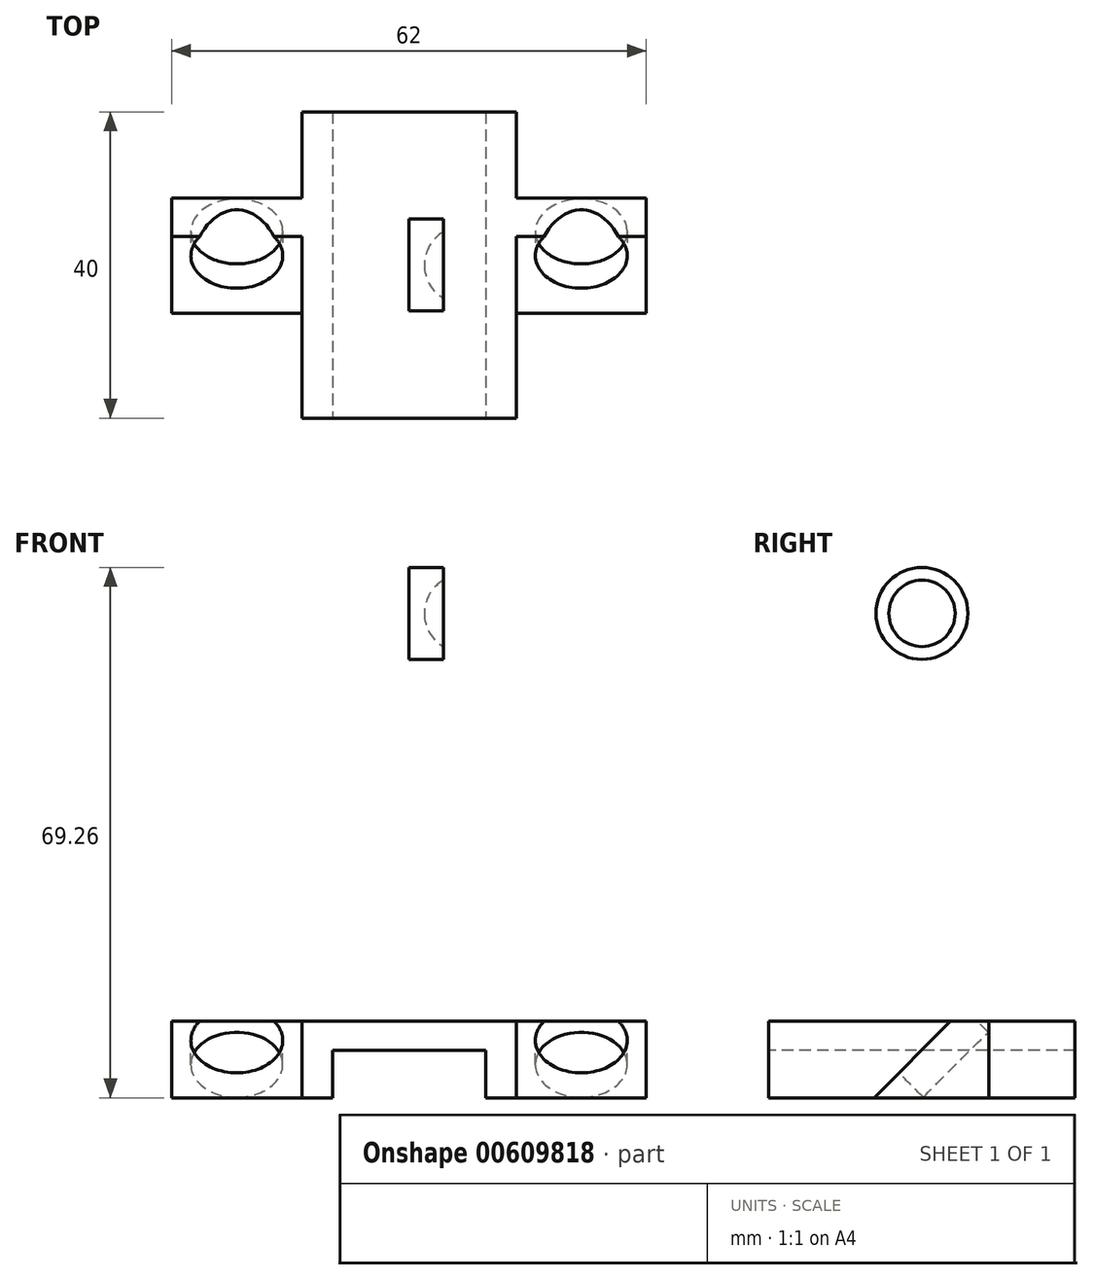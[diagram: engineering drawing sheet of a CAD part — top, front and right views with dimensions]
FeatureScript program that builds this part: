
annotation { "Feature Type Name" : "Feature", "Feature Type Description" : "" }
export const myFeature = defineFeature(function(context is Context, id is Id, definition is map)
    precondition{}
    {
        {
            var Q0;
            Q0=qCreatedBy(makeId("Top.planeOp"),FACE);
            var sketch = newSketch(context, id + "F0", { "sketchPlane" : qUnion([Q0])});
            skLineSegment(sketch, "E0.bottom", {"start": v(14, 20) * mm, "end": v(-14, 20) * mm});
            skLineSegment(sketch, "E0.top", {"start": v(14, -20) * mm, "end": v(-14, -20) * mm});
            skLineSegment(sketch, "E0.left", {"start": v(14, 20) * mm, "end": v(14, 8.72) * mm});
            skLineSegment(sketch, "E0.right", {"start": v(-14, 20) * mm, "end": v(-14, 8.72) * mm});
            skPoint(sketch, "E0.middle", {"position": v(0, 0) * mm});
            skLineSegment(sketch, "E1.bottom", {"start": v(-31, -6.28) * mm, "end": v(-14, -6.28) * mm});
            skLineSegment(sketch, "E1.top", {"start": v(-31, 8.72) * mm, "end": v(-14, 8.72) * mm});
            skLineSegment(sketch, "E1.left", {"start": v(-31, -6.28) * mm, "end": v(-31, 8.72) * mm});
            skLineSegment(sketch, "E1.right", {"start": v(31, -6.28) * mm, "end": v(31, 8.72) * mm});
            skLineSegment(sketch, "E2.trimOffspring", {"start": v(14, 8.72) * mm, "end": v(31, 8.72) * mm});
            skLineSegment(sketch, "E3.trimOffspring", {"start": v(-14, -6.28) * mm, "end": v(-14, -20) * mm});
            skLineSegment(sketch, "E4.trimOffspring", {"start": v(14, -6.28) * mm, "end": v(31, -6.28) * mm});
            skLineSegment(sketch, "E5.trimOffspring", {"start": v(14, -6.28) * mm, "end": v(14, -20) * mm});
            skSolve(sketch);
        }
        {
            var Q0;
            Q0=makeQuery(id+"F0.imprint","IMPRINT",FACE,{"disambiguationData":[TD([[makeQuery(id+"F0.imprint","IMPRINT",EDGE,{"derivedFrom":sQuery(id+"F0.wireOp",EDGE,"E0.bottom")}),1.0]])]});
            extrude(context, id + "F1", {"entities" : qUnion([Q0]), "depth" : 10 * mm, "offsetDistance" : 25 * mm});
        }
        {
            var Q0;
            Q0=makeQuery(id+"F1.opExtrude","SWEPT_FACE",FACE,{"disambiguationData":[OSD([sQuery(id+"F0.wireOp",EDGE,"E0.top")])]});
            var sketch = newSketch(context, id + "F2", { "sketchPlane" : qUnion([Q0])});
            skLineSegment(sketch, "E6.bottom", {"start": v(-10, 0) * mm, "end": v(10, 0) * mm});
            skLineSegment(sketch, "E6.top", {"start": v(-10, 6.21) * mm, "end": v(10, 6.21) * mm});
            skLineSegment(sketch, "E6.left", {"start": v(-10, 0) * mm, "end": v(-10, 6.21) * mm});
            skLineSegment(sketch, "E6.right", {"start": v(10, 0) * mm, "end": v(10, 6.21) * mm});
            skSolve(sketch);
        }
        {
            var Q0;
            Q0=makeQuery(id+"F2.imprint","IMPRINT",FACE,{"disambiguationData":[TD([[makeQuery(id+"F2.imprint","IMPRINT",EDGE,{"derivedFrom":sQuery(id+"F2.wireOp",EDGE,"E6.bottom")}),-1.0]])]});
            extrude(context, id + "F3", {"entities" : qUnion([Q0]), "operationType" : NewBodyOperationType.REMOVE, "endBound" : BoundingType.THROUGH_ALL, "oppositeDirection" : true, "depth" : 25 * mm, "offsetDistance" : 25 * mm});
        }
        {
            var Q0;
            Q0=makeQuery(id+"F1.opExtrude","SWEPT_FACE",FACE,{"disambiguationData":[OSD([sQuery(id+"F0.wireOp",EDGE,"E1.right")])]});
            var sketch = newSketch(context, id + "F4", { "sketchPlane" : qUnion([Q0])});
            skLineSegment(sketch, "E7", {"start": v(-6.28, 0) * mm, "end": v(3.72, 10) * mm});
            skLineSegment(sketch, "E8", {"start": v(-6.28, 0) * mm, "end": v(-6.28, 10) * mm});
            skLineSegment(sketch, "E9", {"start": v(-6.28, 10) * mm, "end": v(3.72, 10) * mm});
            skLineSegment(sketch, "E10", {"start": v(8.72, 0) * mm, "end": v(1.22, 7.5) * mm});
            skPoint(sketch, "E11", {"position": v(1.22, 7.5) * mm});
            skSolve(sketch);
        }
        {
            var Q0;
            Q0=makeQuery(id+"F4.imprint","IMPRINT",FACE,{"disambiguationData":[TD([[makeQuery(id+"F4.imprint","IMPRINT",EDGE,{"derivedFrom":sQuery(id+"F4.wireOp",EDGE,"E7")}),1.0]])]});
            extrude(context, id + "F5", {"entities" : qUnion([Q0]), "operationType" : NewBodyOperationType.REMOVE, "oppositeDirection" : true, "depth" : 17 * mm, "offsetDistance" : 25 * mm});
        }
        {
            var Q0;
            Q0=makeQuery(id+"F5.boolean.opBoolean","COPY",FACE,{"derivedFrom":makeQuery(id+"F5.opExtrude","SWEPT_FACE",FACE,{"disambiguationData":[OSD([sQuery(id+"F4.wireOp",EDGE,"E7")])]})});
            var sketch = newSketch(context, id + "F6", { "sketchPlane" : qUnion([Q0])});
            skPoint(sketch, "E12", {"position": v(22.5, 6.17) * mm});
            skLineSegment(sketch, "E13.0", {"start": v(31, 2.63) * mm, "end": v(31, 9.7) * mm});
            skLineSegment(sketch, "E14.0", {"start": v(14, 9.7) * mm, "end": v(31, 9.7) * mm});
            skCircle(sketch, "E15", {"center": v(22.5, 6.17) * mm, "radius": 6 * mm});
            skSolve(sketch);
        }
        {
            var Q0;
            {var subQ0=sQuery(id+"F6.wireOp",EDGE,"E15");var subQ1=sQuery(id+"F6.wireOp",EDGE,"E14.0");var subQ2=makeQuery(id+"F6.imprint","INTERSECT",VERTEX,{"disambiguationData":[OD(0.0)],"derivedFrom":[subQ1,subQ0]});Q0=makeQuery(id+"F6.imprint","IMPRINT",FACE,{"disambiguationData":[TD([[makeQuery(id+"F6.imprint","IMPRINT",EDGE,{"disambiguationData":[TD([[subQ2,-1.0]])],"derivedFrom":subQ1}),-1.0]])]});}
            var Q1;
            {var subQ0=sQuery(id+"F6.wireOp",EDGE,"E15");var subQ1=sQuery(id+"F6.wireOp",EDGE,"E14.0");var subQ2=makeQuery(id+"F6.imprint","INTERSECT",VERTEX,{"disambiguationData":[OD(0.0)],"derivedFrom":[subQ1,subQ0]});Q1=makeQuery(id+"F6.imprint","IMPRINT",FACE,{"disambiguationData":[TD([[makeQuery(id+"F6.imprint","IMPRINT",EDGE,{"disambiguationData":[TD([[subQ2,-1.0]])],"derivedFrom":subQ1}),1.0]])]});}
            extrude(context, id + "F7", {"entities" : qUnion([Q0, Q1]), "operationType" : NewBodyOperationType.REMOVE, "oppositeDirection" : true, "depth" : 4.5 * mm, "offsetDistance" : 25 * mm});
        }
        {
            var Q0;
            Q0=makeQuery(id+"F1.opExtrude","SWEPT_FACE",FACE,{"disambiguationData":[OSD([sQuery(id+"F0.wireOp",EDGE,"E1.left")])]});
            var sketch = newSketch(context, id + "F8", { "sketchPlane" : qUnion([Q0])});
            skLineSegment(sketch, "E16", {"start": v(6.28, 0) * mm, "end": v(-3.72, 10) * mm});
            skLineSegment(sketch, "E17", {"start": v(-8.72, 0) * mm, "end": v(-1.22, 7.5) * mm});
            skPoint(sketch, "E18", {"position": v(-3.72, 10) * mm});
            skSolve(sketch);
        }
        {
            var Q0;
            {var subQ1=sQuery(id+"F0.wireOp",EDGE,"E1.left");var subQ2=makeQuery(id+"F1.opExtrude","SWEPT_EDGE",EDGE,{"disambiguationData":[OSD([sQuery(id+"F0.wireOp",EDGE,"E1.bottom"),subQ1])]});Q0=makeQuery(id+"F8.imprint","IMPRINT",FACE,{"disambiguationData":[TD([[makeQuery(id+"F8.imprint","IMPRINT",EDGE,{"derivedFrom":subQ2}),-1.0]])]});}
            extrude(context, id + "F9", {"entities" : qUnion([Q0]), "operationType" : NewBodyOperationType.REMOVE, "oppositeDirection" : true, "depth" : 17 * mm, "offsetDistance" : 25 * mm});
        }
        {
            var Q0;
            Q0=makeQuery(id+"F9.boolean.opBoolean","COPY",FACE,{"derivedFrom":makeQuery(id+"F9.opExtrude","SWEPT_FACE",FACE,{"disambiguationData":[OSD([sQuery(id+"F8.wireOp",EDGE,"E16")])]})});
            var sketch = newSketch(context, id + "F10", { "sketchPlane" : qUnion([Q0])});
            skPoint(sketch, "E19", {"position": v(-22.5, 6.17) * mm});
            skCircle(sketch, "E20", {"center": v(-22.5, 6.17) * mm, "radius": 6 * mm});
            skSolve(sketch);
        }
        {
            var Q0;
            {var subQ0=sQuery(id+"F10.wireOp",EDGE,"E20");var subQ1=makeQuery(id+"F9.boolean.opBoolean","COPY",EDGE,{"derivedFrom":makeQuery(id+"F9.opExtrude","SWEPT_EDGE",EDGE,{"disambiguationData":[OSD([sQuery(id+"F0.wireOp",EDGE,"E1.left"),sQuery(id+"F8.wireOp",EDGE,"E16")])]})});var subQ2=makeQuery(id+"F10.imprint","INTERSECT",VERTEX,{"disambiguationData":[OD(0.0)],"derivedFrom":[subQ1,subQ0]});Q0=makeQuery(id+"F10.imprint","IMPRINT",FACE,{"disambiguationData":[TD([[makeQuery(id+"F10.imprint","IMPRINT",EDGE,{"disambiguationData":[TD([[subQ2,-1.0]])],"derivedFrom":subQ0}),1.0]])]});}
            var Q1;
            {var subQ0=sQuery(id+"F10.wireOp",EDGE,"E20");var subQ1=makeQuery(id+"F9.boolean.opBoolean","COPY",EDGE,{"derivedFrom":makeQuery(id+"F9.opExtrude","SWEPT_EDGE",EDGE,{"disambiguationData":[OSD([sQuery(id+"F0.wireOp",EDGE,"E1.left"),sQuery(id+"F8.wireOp",EDGE,"E16")])]})});var subQ2=makeQuery(id+"F10.imprint","INTERSECT",VERTEX,{"disambiguationData":[OD(0.0)],"derivedFrom":[subQ1,subQ0]});Q1=makeQuery(id+"F10.imprint","IMPRINT",FACE,{"disambiguationData":[TD([[makeQuery(id+"F10.imprint","IMPRINT",EDGE,{"disambiguationData":[TD([[subQ2,1.0]])],"derivedFrom":subQ0}),1.0]])]});}
            extrude(context, id + "F11", {"entities" : qUnion([Q0, Q1]), "operationType" : NewBodyOperationType.REMOVE, "oppositeDirection" : true, "depth" : 4.5 * mm, "offsetDistance" : 25 * mm});
        }
        {
            var Q0;
            Q0=qCreatedBy(makeId("Front.planeOp"),FACE);
            var sketch = newSketch(context, id + "F12", { "sketchPlane" : qUnion([Q0])});
            skLineSegment(sketch, "E21.bottom", {"start": v(0, 69.26) * mm, "end": v(4.5, 69.26) * mm});
            skLineSegment(sketch, "E21.left", {"start": v(0, 69.26) * mm, "end": v(0, 63.26) * mm});
            skLineSegment(sketch, "E21.right", {"start": v(4.5, 69.26) * mm, "end": v(4.5, 67.6) * mm});
            skArc(sketch, "E22", {"start": v(4.5, 67.6) * mm, "mid": v(2.67, 65.76) * mm, "end": v(2, 63.26) * mm});
            skLineSegment(sketch, "E23", {"start": v(0, 63.26) * mm, "end": v(2, 63.26) * mm});
            skPoint(sketch, "E23.startSnap0", {"position": v(0, 63.26) * mm});
            skSolve(sketch);
        }
        {
            var Q0;
            Q0=makeQuery(id+"F12.imprint","IMPRINT",FACE,{"disambiguationData":[TD([[makeQuery(id+"F12.imprint","IMPRINT",EDGE,{"derivedFrom":sQuery(id+"F12.wireOp",EDGE,"E21.bottom")}),-1.0]])]});
            var Q1;
            Q1=sQuery(id+"F12.wireOp",EDGE,"E23");
            revolve(context, id + "F13", {"entities" : qUnion([Q0]), "axis" : qUnion([Q1]), "revolveType" : RevolveType.FULL});
        }
    });
